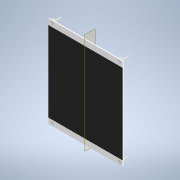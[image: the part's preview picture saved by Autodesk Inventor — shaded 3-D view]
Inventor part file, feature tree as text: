
AUTODESK INVENTOR PART (.ipt)
format: ipt  version: 2022 (Build 260153000, 153)  size: 357,376 bytes
history: native  units: in
note: dims shown in document units (in); Inventor stores cm internally (conversion verified against a paired STEP export)
features: other x10, plane x1
ambient origin geometry x8: Origin, YZ Plane, XZ Plane, XY Plane, X Axis, Y Axis, Z Axis, Center Point
bodies: Solid1 (feature_tree), Solid2 (feature_tree), Solid3 (feature_tree), Solid4 (feature_tree), Solid5 (feature_tree), Solid6 (feature_tree), Solid7 (feature_tree), Solid8 (feature_tree), Solid9 (feature_tree), Solid10 (feature_tree)
feature tree (11):
  plane  "Work Plane1"
  other  "Heatbed_1:1"
  other  "Bed Level Screw_1:1"
  other  "Bed Level Screw_1:2"
  other  "Bed Level Screw_1:3"
  other  "Bed Level Screw_1:4"
  other  "Bed Spring Cap_1:1"
  other  "Bed Spring Cap_1:2"
  other  "Bed Spring Cap_1:3"
  other  "Bed Spring Cap_1:4"
  other  "Print Surface_1:1"
